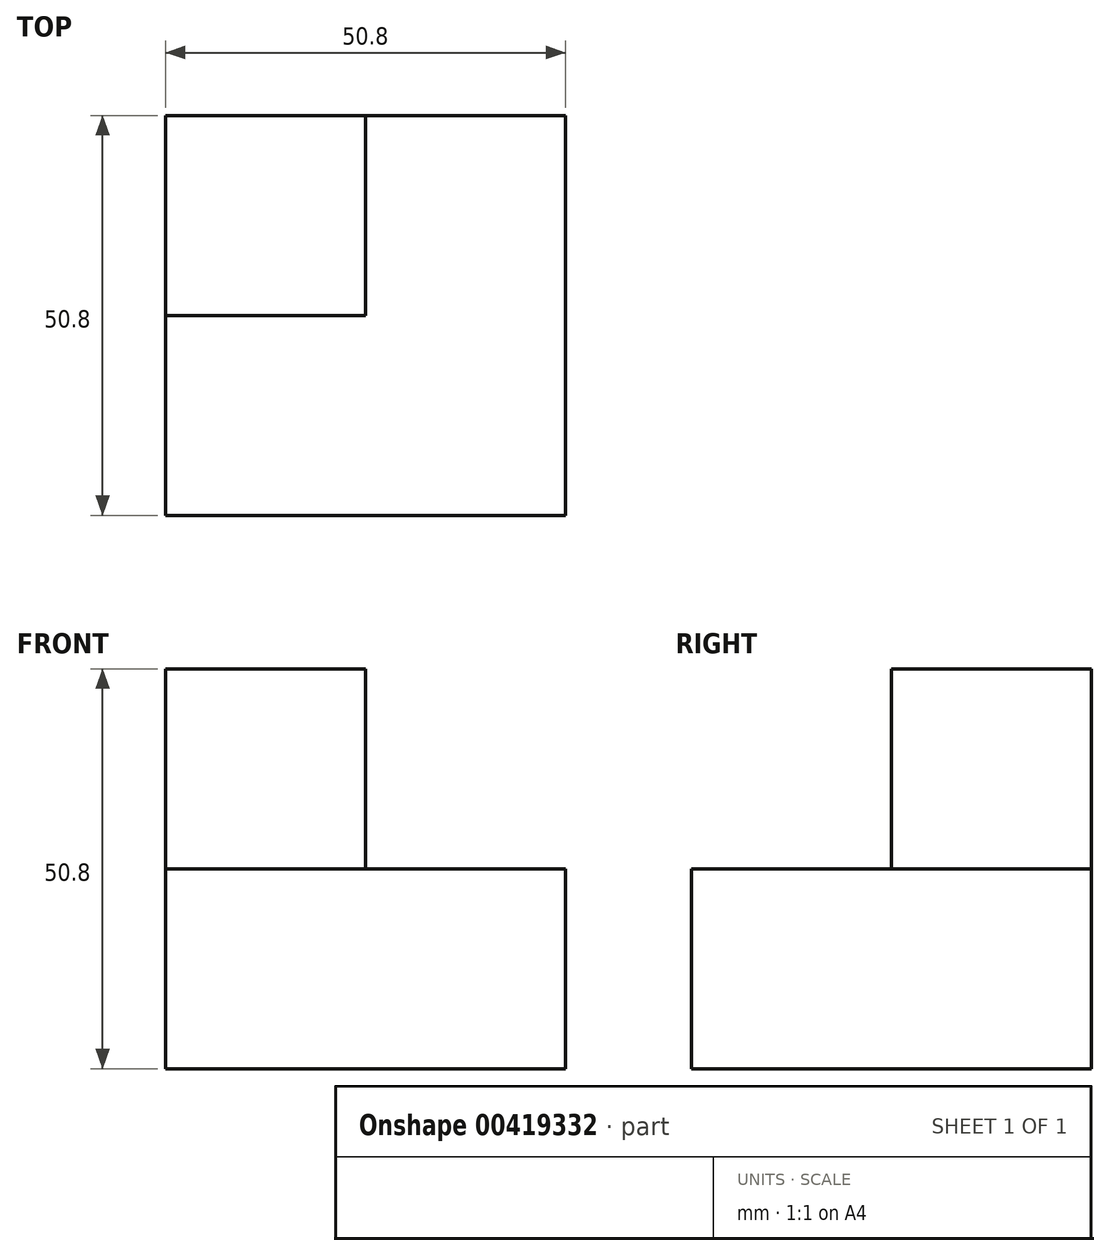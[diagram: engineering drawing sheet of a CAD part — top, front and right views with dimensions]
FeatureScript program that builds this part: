
annotation { "Feature Type Name" : "Feature", "Feature Type Description" : "" }
export const myFeature = defineFeature(function(context is Context, id is Id, definition is map)
    precondition{}
    {
        {
            var Q0;
            Q0=qCreatedBy(makeId("Front.planeOp"),FACE);
            var sketch = newSketch(context, id + "F0", { "sketchPlane" : qUnion([Q0])});
            skLineSegment(sketch, "E0.bottom", {"start": v(0, 0) * mm, "end": v(-50.8, 0) * mm});
            skLineSegment(sketch, "E0.top", {"start": v(0, 25.4) * mm, "end": v(-50.8, 25.4) * mm});
            skLineSegment(sketch, "E0.left", {"start": v(0, 0) * mm, "end": v(0, 25.4) * mm});
            skLineSegment(sketch, "E0.right", {"start": v(-50.8, 0) * mm, "end": v(-50.8, 25.4) * mm});
            skSolve(sketch);
        }
        {
            var Q0;
            Q0 = qSketchRegion(id + "F0", true);
            extrude(context, id + "F1", {"entities" : qUnion([Q0]), "depth" : 50.8 * mm});
        }
        {
            var Q0;
            Q0=makeQuery(id+"F1.opExtrude","SWEPT_FACE",FACE,{"disambiguationData":[OSD([sQuery(id+"F0.wireOp",EDGE,"E0.top")])]});
            var sketch = newSketch(context, id + "F2", { "sketchPlane" : qUnion([Q0])});
            skLineSegment(sketch, "E1.bottom", {"start": v(-50.8, 0) * mm, "end": v(-25.4, 0) * mm});
            skLineSegment(sketch, "E1.top", {"start": v(-50.8, -25.4) * mm, "end": v(-25.4, -25.4) * mm});
            skLineSegment(sketch, "E1.left", {"start": v(-50.8, 0) * mm, "end": v(-50.8, -25.4) * mm});
            skLineSegment(sketch, "E1.right", {"start": v(-25.4, 0) * mm, "end": v(-25.4, -25.4) * mm});
            skSolve(sketch);
        }
        {
            var Q0;
            Q0=makeQuery(id+"F2.imprint","IMPRINT",FACE,{"disambiguationData":[TD([[makeQuery(id+"F2.imprint","IMPRINT",EDGE,{"derivedFrom":sQuery(id+"F2.wireOp",EDGE,"E1.bottom")}),1.0]])]});
            extrude(context, id + "F3", {"entities" : qUnion([Q0]), "operationType" : NewBodyOperationType.ADD, "depth" : 25.4 * mm});
        }
    });
